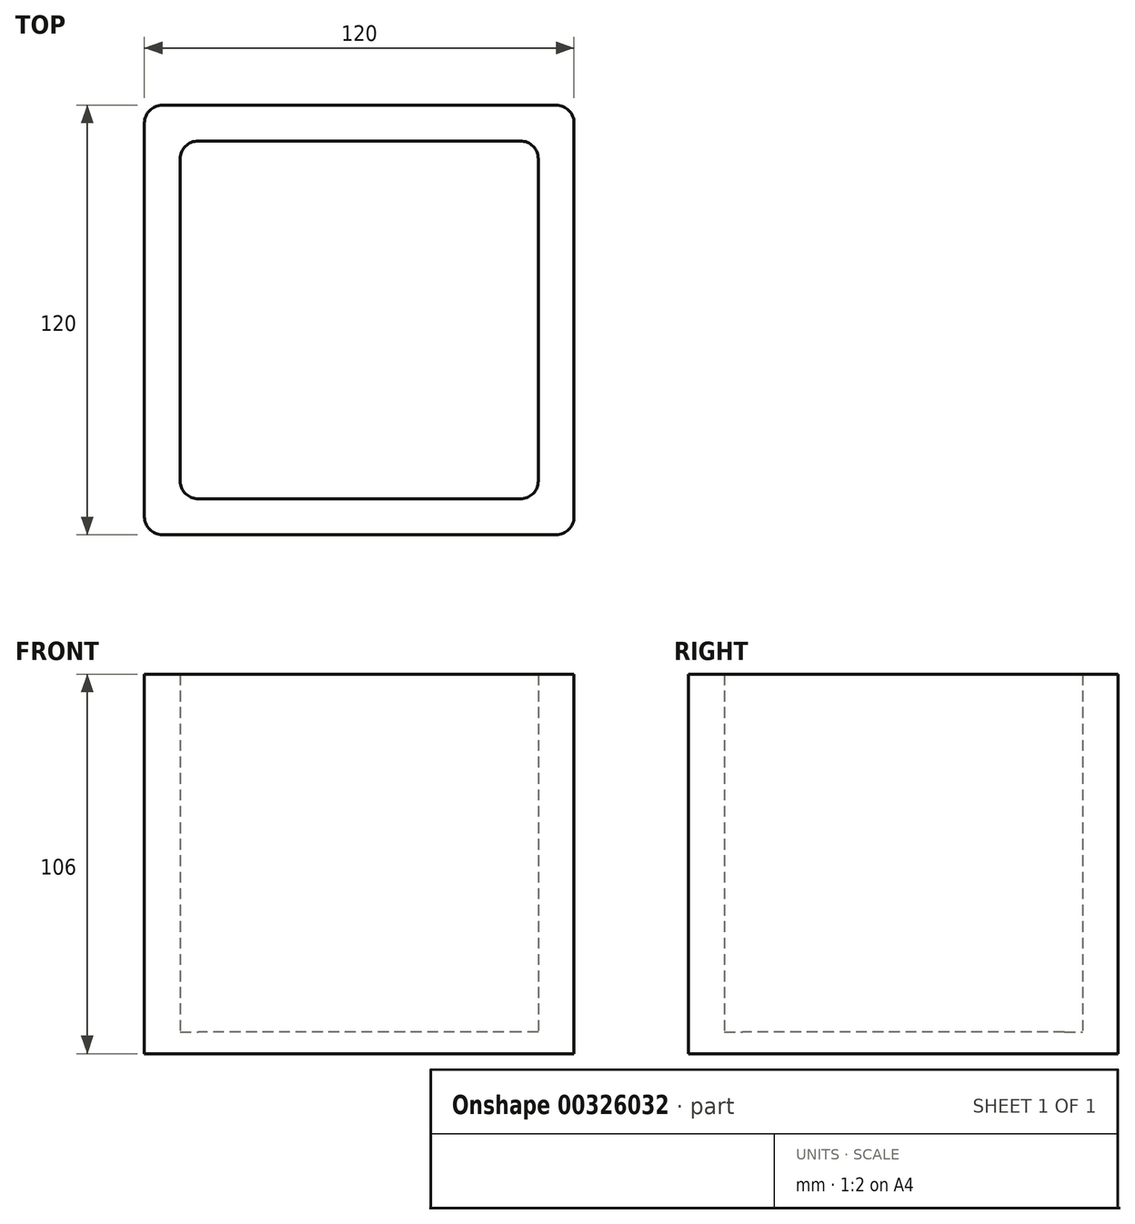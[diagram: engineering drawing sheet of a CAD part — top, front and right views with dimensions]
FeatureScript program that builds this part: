
annotation { "Feature Type Name" : "Feature", "Feature Type Description" : "" }
export const myFeature = defineFeature(function(context is Context, id is Id, definition is map)
    precondition{}
    {
        {
            var Q0;
            Q0=qCreatedBy(makeId("Top.planeOp"),FACE);
            var sketch = newSketch(context, id + "F0", { "sketchPlane" : qUnion([Q0])});
            skLineSegment(sketch, "E0.bottom", {"start": v(45, 50) * mm, "end": v(-45, 50) * mm});
            skLineSegment(sketch, "E0.top", {"start": v(45, -50) * mm, "end": v(-45, -50) * mm});
            skLineSegment(sketch, "E0.left", {"start": v(50, 45) * mm, "end": v(50, -45) * mm});
            skLineSegment(sketch, "E0.right", {"start": v(-50, 45) * mm, "end": v(-50, -45) * mm});
            skPoint(sketch, "E0.middle", {"position": v(0, 0) * mm});
            skLineSegment(sketch, "E1.0", {"start": v(55, 60) * mm, "end": v(-55, 60) * mm});
            skLineSegment(sketch, "E1.1", {"start": v(60, 55) * mm, "end": v(60, -55) * mm});
            skLineSegment(sketch, "E1.2", {"start": v(55, -60) * mm, "end": v(-55, -60) * mm});
            skLineSegment(sketch, "E1.3", {"start": v(-60, 55) * mm, "end": v(-60, -55) * mm});
            skPoint(sketch, "E2.visualSharp", {"position": v(-60, 60) * mm});
            skArc(sketch, "E2.filletArc", {"start": v(-55, 60) * mm, "mid": v(-58.54, 58.54) * mm, "end": v(-60, 55) * mm});
            skPoint(sketch, "E3.visualSharp", {"position": v(60, 60) * mm});
            skArc(sketch, "E3.filletArc", {"start": v(60, 55) * mm, "mid": v(58.54, 58.54) * mm, "end": v(55, 60) * mm});
            skPoint(sketch, "E4.visualSharp", {"position": v(60, -60) * mm});
            skArc(sketch, "E4.filletArc", {"start": v(55, -60) * mm, "mid": v(58.54, -58.54) * mm, "end": v(60, -55) * mm});
            skPoint(sketch, "E5.visualSharp", {"position": v(-60, -60) * mm});
            skArc(sketch, "E5.filletArc", {"start": v(-60, -55) * mm, "mid": v(-58.54, -58.54) * mm, "end": v(-55, -60) * mm});
            skPoint(sketch, "E6.visualSharp", {"position": v(-50, -50) * mm});
            skArc(sketch, "E6.filletArc", {"start": v(-50, -45) * mm, "mid": v(-48.54, -48.54) * mm, "end": v(-45, -50) * mm});
            skPoint(sketch, "E7.visualSharp", {"position": v(-50, 50) * mm});
            skArc(sketch, "E7.filletArc", {"start": v(-45, 50) * mm, "mid": v(-48.54, 48.54) * mm, "end": v(-50, 45) * mm});
            skPoint(sketch, "E8.visualSharp", {"position": v(50, 50) * mm});
            skArc(sketch, "E8.filletArc", {"start": v(50, 45) * mm, "mid": v(48.54, 48.54) * mm, "end": v(45, 50) * mm});
            skPoint(sketch, "E9.visualSharp", {"position": v(50, -50) * mm});
            skArc(sketch, "E9.filletArc", {"start": v(45, -50) * mm, "mid": v(48.54, -48.54) * mm, "end": v(50, -45) * mm});
            skSolve(sketch);
        }
        {
            var Q0;
            Q0 = qSketchRegion(id + "F0", true);
            var Q1;
            Q1=makeQuery(id+"F0.imprint","IMPRINT",FACE,{"disambiguationData":[TD([[makeQuery(id+"F0.imprint","IMPRINT",EDGE,{"derivedFrom":sQuery(id+"F0.wireOp",EDGE,"E0.bottom")}),1.0]])]});
            extrude(context, id + "F1", {"entities" : qUnion([Q0, Q1]), "depth" : 6 * mm});
        }
        {
            var Q0;
            Q0=makeQuery(id+"F1.opExtrude","CAP_FACE",FACE,{"disambiguationData":[OSD([sQuery(id+"F0.wireOp",EDGE,"E1.0"),sQuery(id+"F0.wireOp",EDGE,"E1.1"),sQuery(id+"F0.wireOp",EDGE,"E1.2"),sQuery(id+"F0.wireOp",EDGE,"E1.3"),sQuery(id+"F0.wireOp",EDGE,"E2.filletArc"),sQuery(id+"F0.wireOp",EDGE,"E3.filletArc"),sQuery(id+"F0.wireOp",EDGE,"E4.filletArc"),sQuery(id+"F0.wireOp",EDGE,"E5.filletArc")])],"isStart":false});
            var sketch = newSketch(context, id + "F2", { "sketchPlane" : qUnion([Q0])});
            skLineSegment(sketch, "E10.0.0", {"start": v(-55, -60) * mm, "end": v(55, -60) * mm});
            skArc(sketch, "E10.0.1", {"start": v(55, -60) * mm, "mid": v(58.54, -58.54) * mm, "end": v(60, -55) * mm});
            skLineSegment(sketch, "E10.0.2", {"start": v(60, -55) * mm, "end": v(60, 55) * mm});
            skArc(sketch, "E10.0.3", {"start": v(60, 55) * mm, "mid": v(58.54, 58.54) * mm, "end": v(55, 60) * mm});
            skLineSegment(sketch, "E10.0.4", {"start": v(55, 60) * mm, "end": v(-55, 60) * mm});
            skArc(sketch, "E10.0.5", {"start": v(-55, 60) * mm, "mid": v(-58.54, 58.54) * mm, "end": v(-60, 55) * mm});
            skLineSegment(sketch, "E10.0.6", {"start": v(-60, 55) * mm, "end": v(-60, -55) * mm});
            skArc(sketch, "E10.0.7", {"start": v(-60, -55) * mm, "mid": v(-58.54, -58.54) * mm, "end": v(-55, -60) * mm});
            skLineSegment(sketch, "E11.0", {"start": v(-50, 45) * mm, "end": v(-50, -45) * mm});
            skLineSegment(sketch, "E12.0", {"start": v(45, 50) * mm, "end": v(-45, 50) * mm});
            skArc(sketch, "E13.0", {"start": v(-45, 50) * mm, "mid": v(-48.54, 48.54) * mm, "end": v(-50, 45) * mm});
            skLineSegment(sketch, "E14.0", {"start": v(50, 45) * mm, "end": v(50, -45) * mm});
            skArc(sketch, "E15.0", {"start": v(50, 45) * mm, "mid": v(48.54, 48.54) * mm, "end": v(45, 50) * mm});
            skLineSegment(sketch, "E16.0", {"start": v(45, -50) * mm, "end": v(-45, -50) * mm});
            skArc(sketch, "E17.0", {"start": v(45, -50) * mm, "mid": v(48.54, -48.54) * mm, "end": v(50, -45) * mm});
            skArc(sketch, "E18.0", {"start": v(-50, -45) * mm, "mid": v(-48.54, -48.54) * mm, "end": v(-45, -50) * mm});
            skSolve(sketch);
        }
        {
            var Q0;
            Q0=makeQuery(id+"F2.imprint","IMPRINT",FACE,{"disambiguationData":[TD([[makeQuery(id+"F2.imprint","IMPRINT",EDGE,{"derivedFrom":sQuery(id+"F2.wireOp",EDGE,"E10.0.0")}),-1.0]])]});
            extrude(context, id + "F3", {"entities" : qUnion([Q0]), "operationType" : NewBodyOperationType.ADD, "depth" : 100 * mm});
        }
    });
